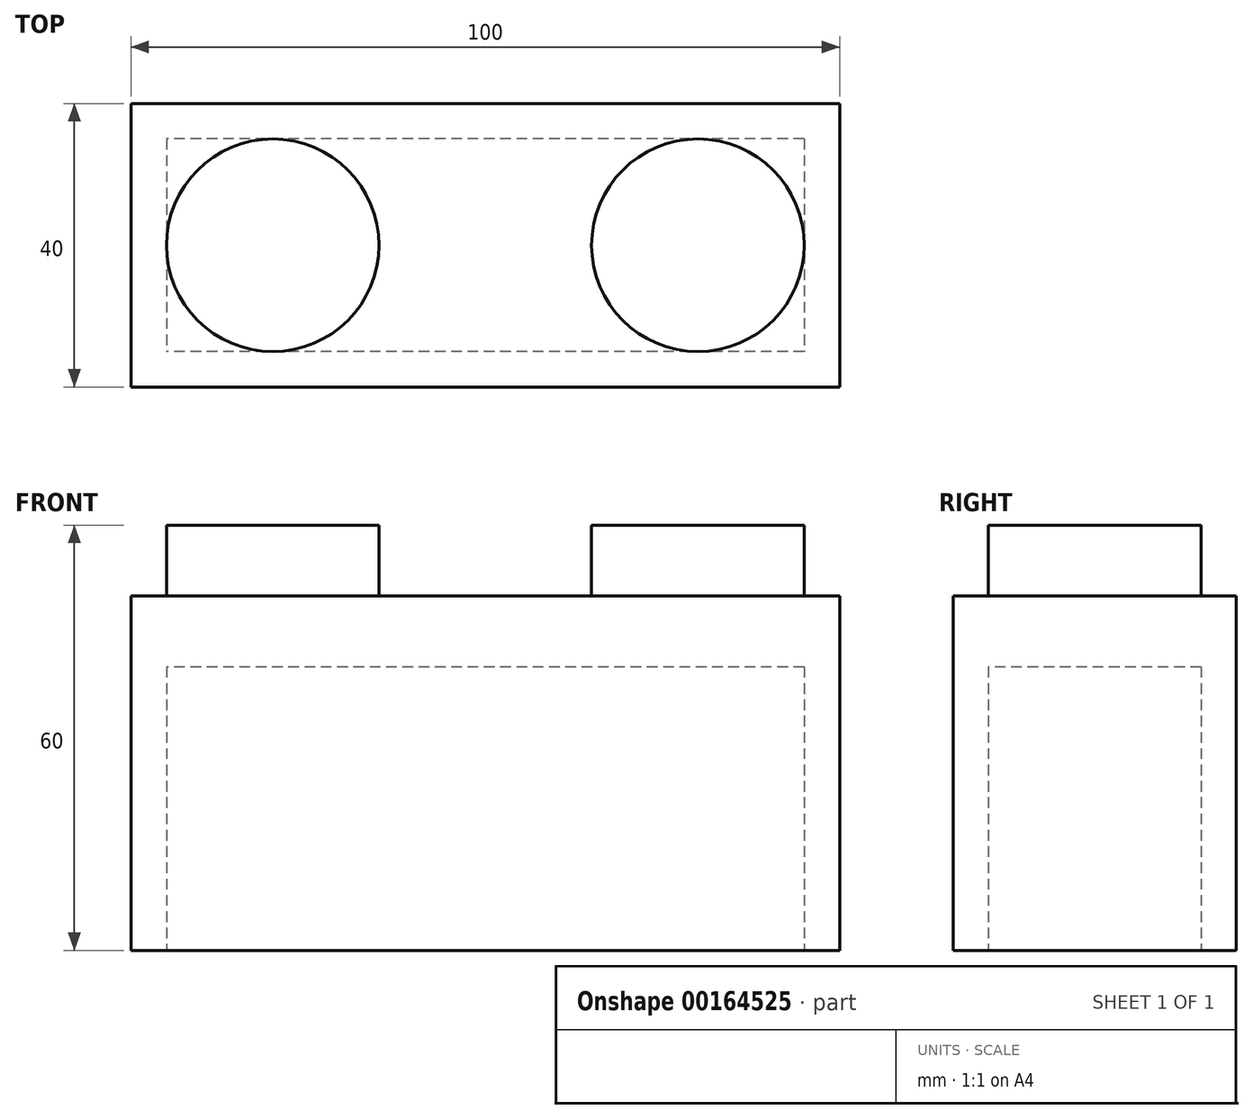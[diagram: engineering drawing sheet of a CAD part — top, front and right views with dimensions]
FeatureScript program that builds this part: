
annotation { "Feature Type Name" : "Feature", "Feature Type Description" : "" }
export const myFeature = defineFeature(function(context is Context, id is Id, definition is map)
    precondition{}
    {
        {
            var Q0;
            Q0=qCreatedBy(makeId("Front.planeOp"),FACE);
            var sketch = newSketch(context, id + "F0", { "sketchPlane" : qUnion([Q0])});
            skLineSegment(sketch, "E0.bottom", {"start": v(50, -25) * mm, "end": v(-50, -25) * mm});
            skLineSegment(sketch, "E0.top", {"start": v(50, 25) * mm, "end": v(-50, 25) * mm});
            skLineSegment(sketch, "E0.left", {"start": v(50, -25) * mm, "end": v(50, 25) * mm});
            skLineSegment(sketch, "E0.right", {"start": v(-50, -25) * mm, "end": v(-50, 25) * mm});
            skPoint(sketch, "E0.middle", {"position": v(0, 0) * mm});
            skSolve(sketch);
        }
        {
            var Q0;
            Q0 = qSketchRegion(id + "F0", true);
            extrude(context, id + "F1", {"entities" : qUnion([Q0]), "depth" : 40 * mm});
        }
        {
            var Q0;
            Q0=makeQuery(id+"F1.opExtrude","SWEPT_FACE",FACE,{"disambiguationData":[OSD([sQuery(id+"F0.wireOp",EDGE,"E0.top")])]});
            var sketch = newSketch(context, id + "F2", { "sketchPlane" : qUnion([Q0])});
            skPoint(sketch, "E1.endSnap0", {"position": v(50, -20) * mm});
            skCircle(sketch, "E2", {"center": v(-30, -20) * mm, "radius": 15 * mm});
            skCircle(sketch, "E3", {"center": v(30, -20) * mm, "radius": 15 * mm});
            skPoint(sketch, "E1.end.orphan", {"position": v(45, -20) * mm});
            skPoint(sketch, "E1.start.orphan", {"position": v(50, -20) * mm});
            skPoint(sketch, "E4.end.orphan", {"position": v(-45, -20) * mm});
            skPoint(sketch, "E4.start.orphan", {"position": v(-50, -20) * mm});
            skSolve(sketch);
        }
        {
            var Q0;
            Q0 = qSketchRegion(id + "F2", true);
            extrude(context, id + "F3", {"entities" : qUnion([Q0]), "operationType" : NewBodyOperationType.ADD, "depth" : 10 * mm});
        }
        {
            var Q0;
            Q0=makeQuery(id+"F1.opExtrude","SWEPT_FACE",FACE,{"disambiguationData":[OSD([sQuery(id+"F0.wireOp",EDGE,"E0.bottom")])]});
            var sketch = newSketch(context, id + "F4", { "sketchPlane" : qUnion([Q0])});
            skLineSegment(sketch, "E5.bottom", {"start": v(45, 5) * mm, "end": v(-45, 5) * mm});
            skLineSegment(sketch, "E5.top", {"start": v(45, 35) * mm, "end": v(-45, 35) * mm});
            skLineSegment(sketch, "E5.left", {"start": v(45, 5) * mm, "end": v(45, 35) * mm});
            skLineSegment(sketch, "E5.right", {"start": v(-45, 5) * mm, "end": v(-45, 35) * mm});
            skPoint(sketch, "E5.middle", {"position": v(0, 20) * mm});
            skPoint(sketch, "E5.middle.positionSnap0", {"position": v(50, 20) * mm});
            skPoint(sketch, "E5.centerSnap0", {"position": v(50, 20) * mm});
            skSolve(sketch);
        }
        {
            var Q0;
            Q0 = qSketchRegion(id + "F4", true);
            extrude(context, id + "F5", {"entities" : qUnion([Q0]), "operationType" : NewBodyOperationType.REMOVE, "oppositeDirection" : true, "depth" : 40 * mm});
        }
    });
